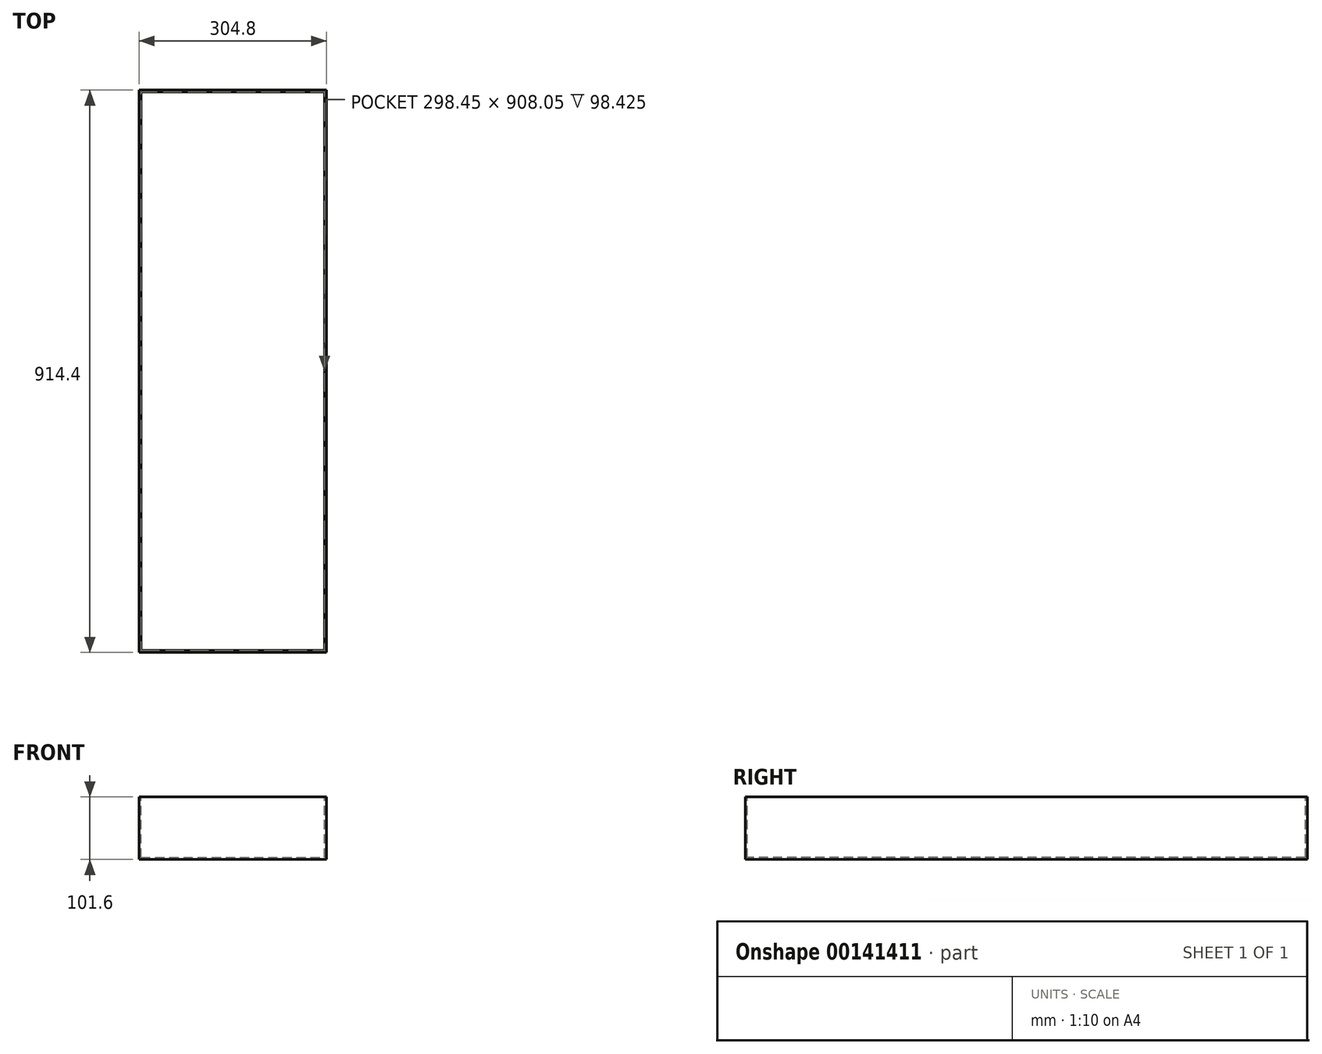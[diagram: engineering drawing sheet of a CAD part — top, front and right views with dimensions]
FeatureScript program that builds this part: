
annotation { "Feature Type Name" : "Feature", "Feature Type Description" : "" }
export const myFeature = defineFeature(function(context is Context, id is Id, definition is map)
    precondition{}
    {
        {
            var Q0;
            Q0=qCreatedBy(makeId("Top.planeOp"),FACE);
            var sketch = newSketch(context, id + "F0", { "sketchPlane" : qUnion([Q0])});
            skLineSegment(sketch, "E0.bottom", {"start": v(-152.4, 457.2) * mm, "end": v(152.4, 457.2) * mm});
            skLineSegment(sketch, "E0.top", {"start": v(-152.4, -457.2) * mm, "end": v(152.4, -457.2) * mm});
            skLineSegment(sketch, "E0.left", {"start": v(-152.4, 457.2) * mm, "end": v(-152.4, -457.2) * mm});
            skLineSegment(sketch, "E0.right", {"start": v(152.4, 457.2) * mm, "end": v(152.4, -457.2) * mm});
            skPoint(sketch, "E0.middle", {"position": v(0, 0) * mm});
            skSolve(sketch);
        }
        {
            var Q0;
            Q0=qSketchRegion(id+"F0",true);
            extrude(context, id + "F1", {"entities" : qUnion([Q0]), "depth" : 101.6 * mm});
        }
        {
            var Q0;
            Q0=makeQuery(id+"F1.opExtrude","CAP_FACE",FACE,{"disambiguationData":[OSD([sQuery(id+"F0.wireOp",EDGE,"E0.bottom"),sQuery(id+"F0.wireOp",EDGE,"E0.top"),sQuery(id+"F0.wireOp",EDGE,"E0.left"),sQuery(id+"F0.wireOp",EDGE,"E0.right")])],"isStart":false});
            var sketch = newSketch(context, id + "F2", { "sketchPlane" : qUnion([Q0])});
            skLineSegment(sketch, "E1.bottom", {"start": v(-149.22, 454.03) * mm, "end": v(149.22, 454.03) * mm});
            skLineSegment(sketch, "E1.top", {"start": v(-149.22, -454.03) * mm, "end": v(149.22, -454.03) * mm});
            skLineSegment(sketch, "E1.left", {"start": v(-149.22, 454.03) * mm, "end": v(-149.23, -454.03) * mm});
            skLineSegment(sketch, "E1.right", {"start": v(149.23, 454.03) * mm, "end": v(149.22, -454.03) * mm});
            skPoint(sketch, "E1.middle", {"position": v(0, 0) * mm});
            skSolve(sketch);
        }
        {
            var Q0;
            Q0=qSketchRegion(id+"F2",true);
            extrude(context, id + "F3", {"entities" : qUnion([Q0]), "operationType" : NewBodyOperationType.REMOVE, "oppositeDirection" : true, "depth" : 98.42 * mm});
        }
    });
